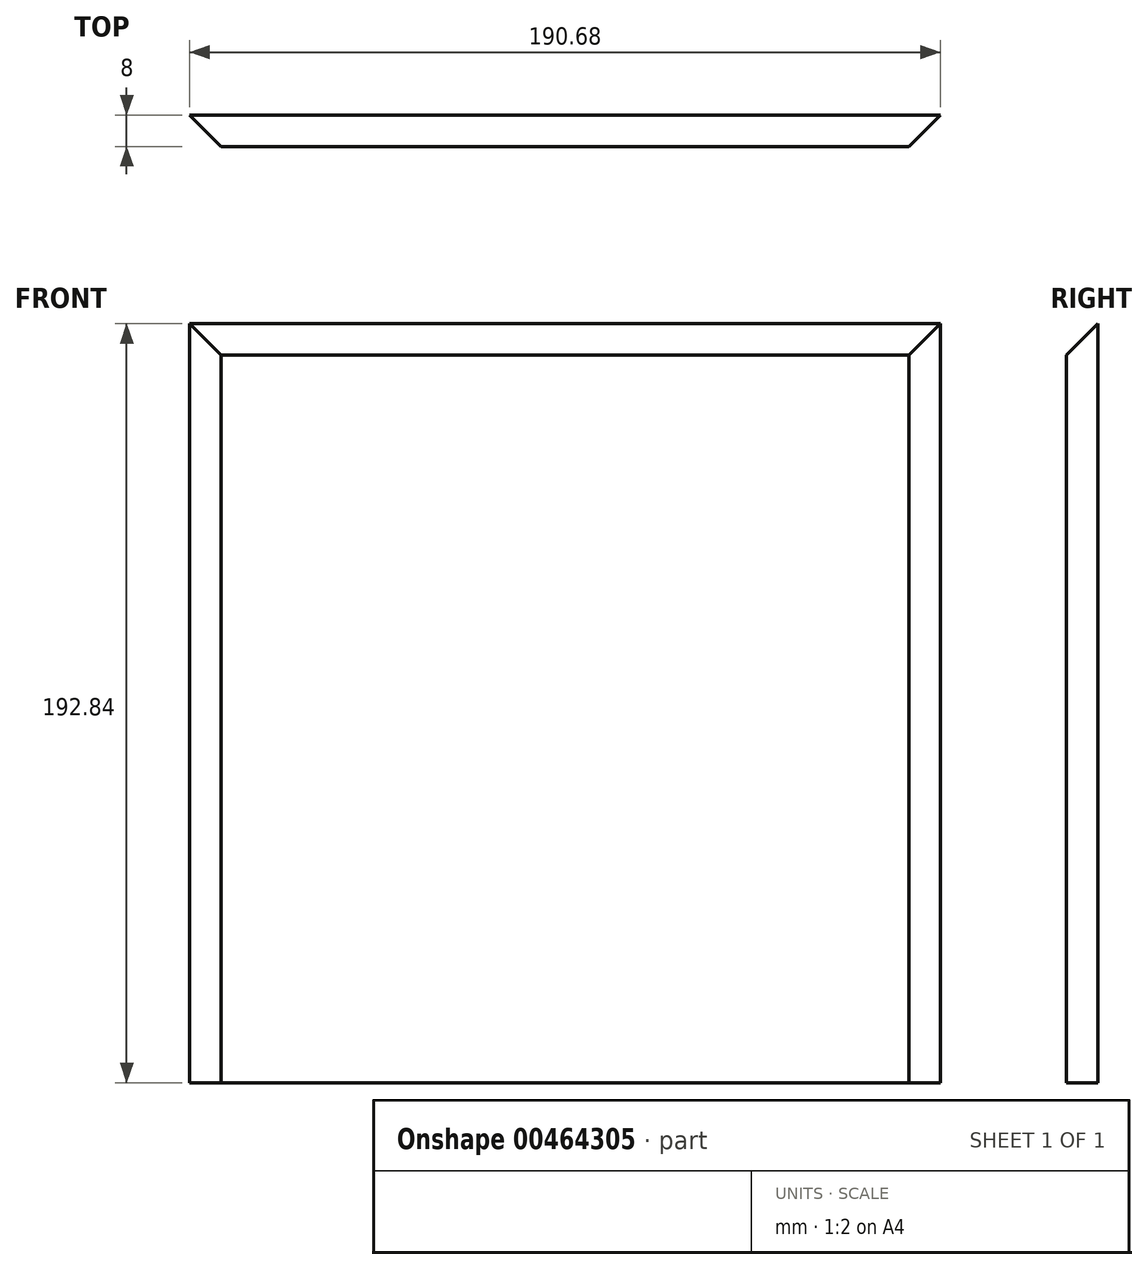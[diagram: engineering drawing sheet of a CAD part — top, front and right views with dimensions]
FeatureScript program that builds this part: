
annotation { "Feature Type Name" : "Feature", "Feature Type Description" : "" }
export const myFeature = defineFeature(function(context is Context, id is Id, definition is map)
    precondition{}
    {
        {
            var Q0;
            Q0=qCreatedBy(makeId("Front.planeOp"),FACE);
            var sketch = newSketch(context, id + "F0", { "sketchPlane" : qUnion([Q0])});
            skLineSegment(sketch, "E0.bottom", {"start": v(97.5, 97.5) * mm, "end": v(-97.5, 97.5) * mm});
            skLineSegment(sketch, "E0.top", {"start": v(97.5, -97.5) * mm, "end": v(-97.5, -97.5) * mm});
            skLineSegment(sketch, "E0.left", {"start": v(97.5, 97.5) * mm, "end": v(97.5, -97.5) * mm});
            skLineSegment(sketch, "E0.right", {"start": v(-97.5, 97.5) * mm, "end": v(-97.5, -97.5) * mm});
            skPoint(sketch, "E0.middle", {"position": v(0, 0) * mm});
            skSolve(sketch);
        }
        {
            var Q0;
            Q0=makeQuery(id+"F0.imprint","IMPRINT",FACE,{"disambiguationData":[TD([[makeQuery(id+"F0.imprint","IMPRINT",EDGE,{"derivedFrom":sQuery(id+"F0.wireOp",EDGE,"E0.bottom")}),1.0]])]});
            extrude(context, id + "F1", {"entities" : qUnion([Q0]), "endBound" : BoundingType.SYMMETRIC, "depth" : 8 * mm});
        }
        {
            var Q0;
            Q0=makeQuery(id+"F1.opExtrude","CAP_EDGE",EDGE,{"disambiguationData":[OSD([sQuery(id+"F0.wireOp",EDGE,"E0.left")])],"isStart":false});
            chamfer(context, id + "F2", {"entities" : qUnion([Q0]), "width" : 10.16 * mm, "tangentPropagation" : true});
        }
        {
            var Q0;
            Q0=makeQuery(id+"F1.opExtrude","CAP_EDGE",EDGE,{"disambiguationData":[OSD([sQuery(id+"F0.wireOp",EDGE,"E0.right")])],"isStart":false});
            chamfer(context, id + "F3", {"entities" : qUnion([Q0]), "width" : 10.16 * mm, "tangentPropagation" : true});
        }
        {
            var Q0;
            Q0=makeQuery(id+"F1.opExtrude","CAP_EDGE",EDGE,{"disambiguationData":[OSD([sQuery(id+"F0.wireOp",EDGE,"E0.bottom")])],"isStart":false});
            chamfer(context, id + "F4", {"entities" : qUnion([Q0]), "width" : 10.16 * mm, "tangentPropagation" : true});
        }
    });
